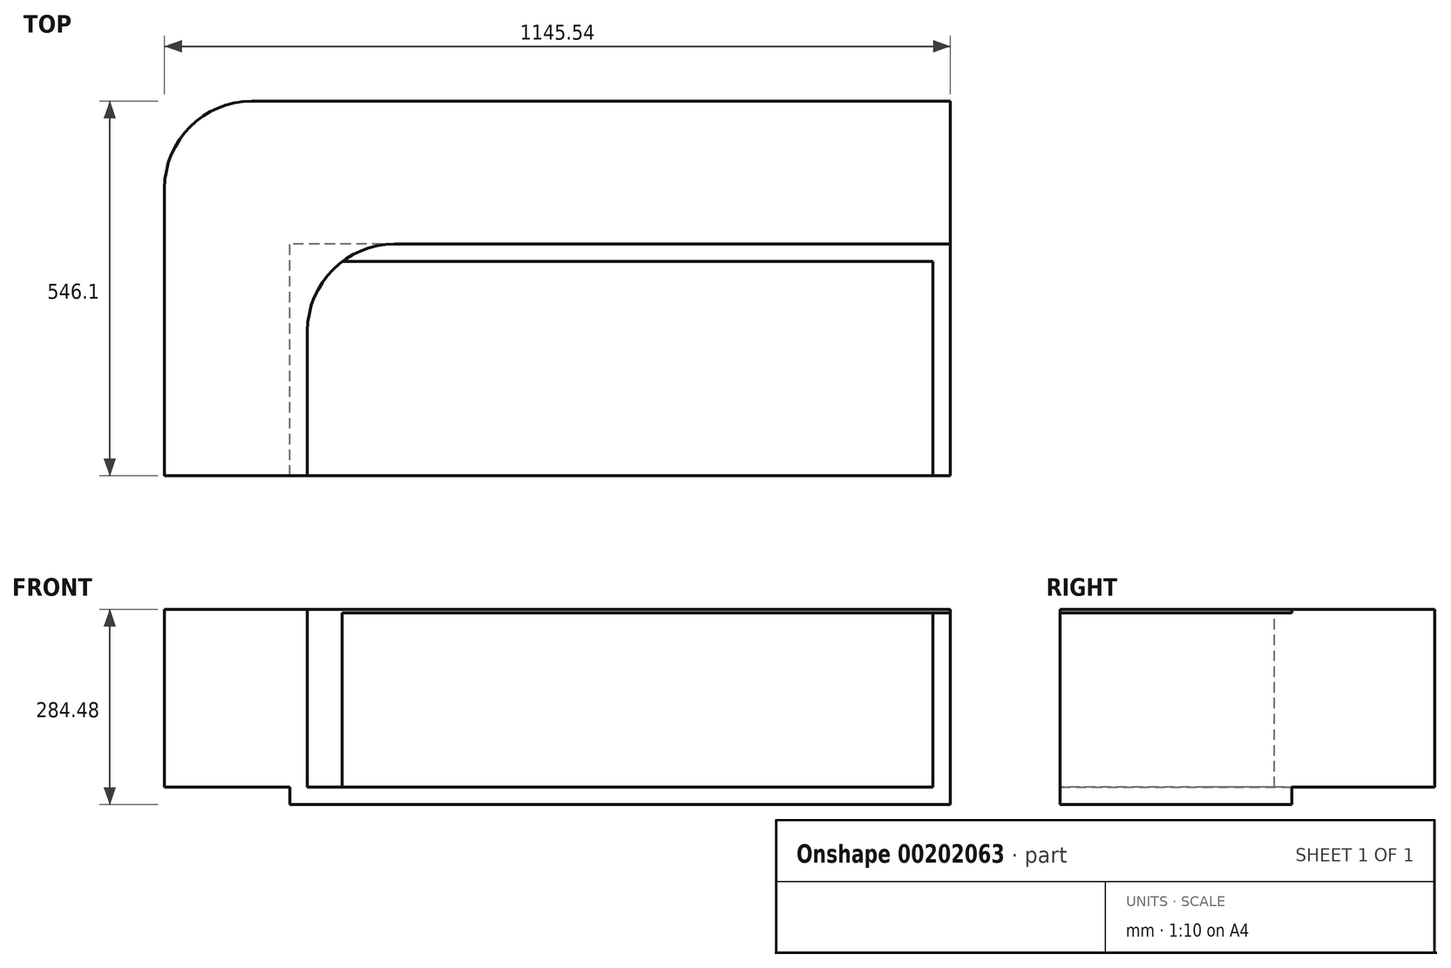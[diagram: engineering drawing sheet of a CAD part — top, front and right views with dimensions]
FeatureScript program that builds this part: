
annotation { "Feature Type Name" : "Feature", "Feature Type Description" : "" }
export const myFeature = defineFeature(function(context is Context, id is Id, definition is map)
    precondition{}
    {
        {
            var Q0;
            Q0=qCreatedBy(makeId("Top.planeOp"),FACE);
            cPlane(context, id + "F0", {"entities" : qUnion([Q0]), "cplaneType" : CPlaneType.OFFSET, "offset" : 101.6 * mm, "oppositeDirection" : true, "width" : 152.4 * mm, "height" : 152.4 * mm});
        }
        {
            var Q0;
            Q0=qCreatedBy(id+"F0.planeOp",FACE);
            var sketch = newSketch(context, id + "F1", { "sketchPlane" : qUnion([Q0])});
            skLineSegment(sketch, "E0.bottom", {"start": v(-468.63, 0) * mm, "end": v(468.63, 0) * mm});
            skLineSegment(sketch, "E0.top", {"start": v(-468.63, 312.42) * mm, "end": v(468.63, 312.42) * mm});
            skLineSegment(sketch, "E0.left", {"start": v(-468.63, 0) * mm, "end": v(-468.63, 312.42) * mm});
            skLineSegment(sketch, "E0.right", {"start": v(468.63, 0) * mm, "end": v(468.63, 312.42) * mm});
            skSolve(sketch);
        }
        {
            var Q0;
            Q0=makeQuery(id+"F1.imprint","IMPRINT",FACE,{"disambiguationData":[TD([[makeQuery(id+"F1.imprint","IMPRINT",EDGE,{"derivedFrom":sQuery(id+"F1.wireOp",EDGE,"E0.bottom")}),1.0]])]});
            extrude(context, id + "F2", {"entities" : qUnion([Q0]), "oppositeDirection" : true, "depth" : 254 * mm});
        }
        {
            var Q0;
            Q0=makeQuery(id+"F2.opExtrude","CAP_FACE",FACE,{"disambiguationData":[OSD([sQuery(id+"F1.wireOp",EDGE,"E0.bottom"),sQuery(id+"F1.wireOp",EDGE,"E0.top"),sQuery(id+"F1.wireOp",EDGE,"E0.left"),sQuery(id+"F1.wireOp",EDGE,"E0.right")])],"isStart":true});
            var Q1;
            Q1=makeQuery(id+"F2.opExtrude","SWEPT_FACE",FACE,{"disambiguationData":[OSD([sQuery(id+"F1.wireOp",EDGE,"E0.bottom")])]});
            var Q2;
            Q2=makeQuery(id+"F2.opExtrude","SWEPT_FACE",FACE,{"disambiguationData":[OSD([sQuery(id+"F1.wireOp",EDGE,"E0.left")])]});
            shell(context, id + "F3", {"entities" : qUnion([Q0, Q1, Q2]), "thickness" : 25.4 * mm, "oppositeDirection" : true});
        }
        {
            var Q0;
            Q0=makeQuery(id+"F2.opExtrude","SWEPT_FACE",FACE,{"disambiguationData":[OSD([sQuery(id+"F1.wireOp",EDGE,"E0.right")])]});
            var sketch = newSketch(context, id + "F4", { "sketchPlane" : qUnion([Q0])});
            skLineSegment(sketch, "E1", {"start": v(0, -152.4) * mm, "end": v(337.82, -152.4) * mm});
            skLineSegment(sketch, "E2", {"start": v(0, -101.6) * mm, "end": v(0, -152.4) * mm});
            skLineSegment(sketch, "E3", {"start": v(0, -101.6) * mm, "end": v(337.82, -101.6) * mm});
            skSolve(sketch);
        }
        {
            var Q0;
            Q0=sQuery(id+"F4.wireOp",EDGE,"E1");
            extrude(context, id + "F5", {"bodyType" : ToolBodyType.SURFACE, "surfaceEntities" : qUnion([Q0]), "oppositeDirection" : true, "depth" : 937.26 * mm});
        }
        {
            var Q0;
            Q0=sQuery(id+"F4.wireOp",EDGE,"E3");
            extrude(context, id + "F6", {"bodyType" : ToolBodyType.SURFACE, "surfaceEntities" : qUnion([Q0]), "oppositeDirection" : true, "depth" : 937.26 * mm});
        }
        {
            var Q0;
            Q0=makeQuery(id+"F6.opExtrude","SWEPT_FACE",FACE,{"disambiguationData":[OSD([sQuery(id+"F4.wireOp",EDGE,"E3")])]});
            var sketch = newSketch(context, id + "F7", { "sketchPlane" : qUnion([Q0])});
            skLineSegment(sketch, "E4", {"start": v(494.03, 337.82) * mm, "end": v(494.03, 546.1) * mm});
            skLineSegment(sketch, "E5", {"start": v(494.03, 546.1) * mm, "end": v(-651.51, 546.1) * mm});
            skLineSegment(sketch, "E6", {"start": v(-651.51, 546.1) * mm, "end": v(-651.51, 0) * mm});
            skLineSegment(sketch, "E7", {"start": v(-651.51, 0) * mm, "end": v(-443.23, 0) * mm});
            skLineSegment(sketch, "E8", {"start": v(-443.23, 0) * mm, "end": v(-443.23, 337.82) * mm});
            skLineSegment(sketch, "E9", {"start": v(-443.23, 337.82) * mm, "end": v(494.03, 337.82) * mm});
            skSolve(sketch);
        }
        {
            var Q0;
            Q0=makeQuery(id+"F7.imprint","IMPRINT",FACE,{"disambiguationData":[TD([[makeQuery(id+"F7.imprint","IMPRINT",EDGE,{"derivedFrom":sQuery(id+"F7.wireOp",EDGE,"E4")}),1.0]])]});
            extrude(context, id + "F8", {"entities" : qUnion([Q0]), "operationType" : NewBodyOperationType.ADD, "oppositeDirection" : true, "depth" : 254 * mm, "hasSecondDirection" : true, "secondDirectionOppositeDirection" : false, "secondDirectionDepth" : 5.08 * mm});
        }
        {
            var Q0;
            Q0=makeQuery(id+"F8.opExtrude","SWEPT_EDGE",EDGE,{"disambiguationData":[OSD([sQuery(id+"F7.wireOp",EDGE,"E5"),sQuery(id+"F7.wireOp",EDGE,"E6")])]});
            var Q1;
            Q1=makeQuery(id+"F3.opShell","OFFSET_EDGE",EDGE,{"disambiguationData":[OSD([sQuery(id+"F1.wireOp",EDGE,"E0.top"),sQuery(id+"F1.wireOp",EDGE,"E0.left")])]});
            fillet(context, id + "F9", {"entities" : qUnion([Q0, Q1]), "radius" : 127 * mm, "tangentPropagation" : true, "allowEdgeOverflow" : false});
        }
        {
            var Q0;
            Q0=makeQuery(id+"F8.opExtrude","SWEPT_EDGE",EDGE,{"disambiguationData":[OSD([sQuery(id+"F7.wireOp",EDGE,"E8"),sQuery(id+"F7.wireOp",EDGE,"E9")])]});
            fillet(context, id + "F10", {"entities" : qUnion([Q0]), "radius" : 127 * mm, "tangentPropagation" : true, "allowEdgeOverflow" : false});
        }
    });
